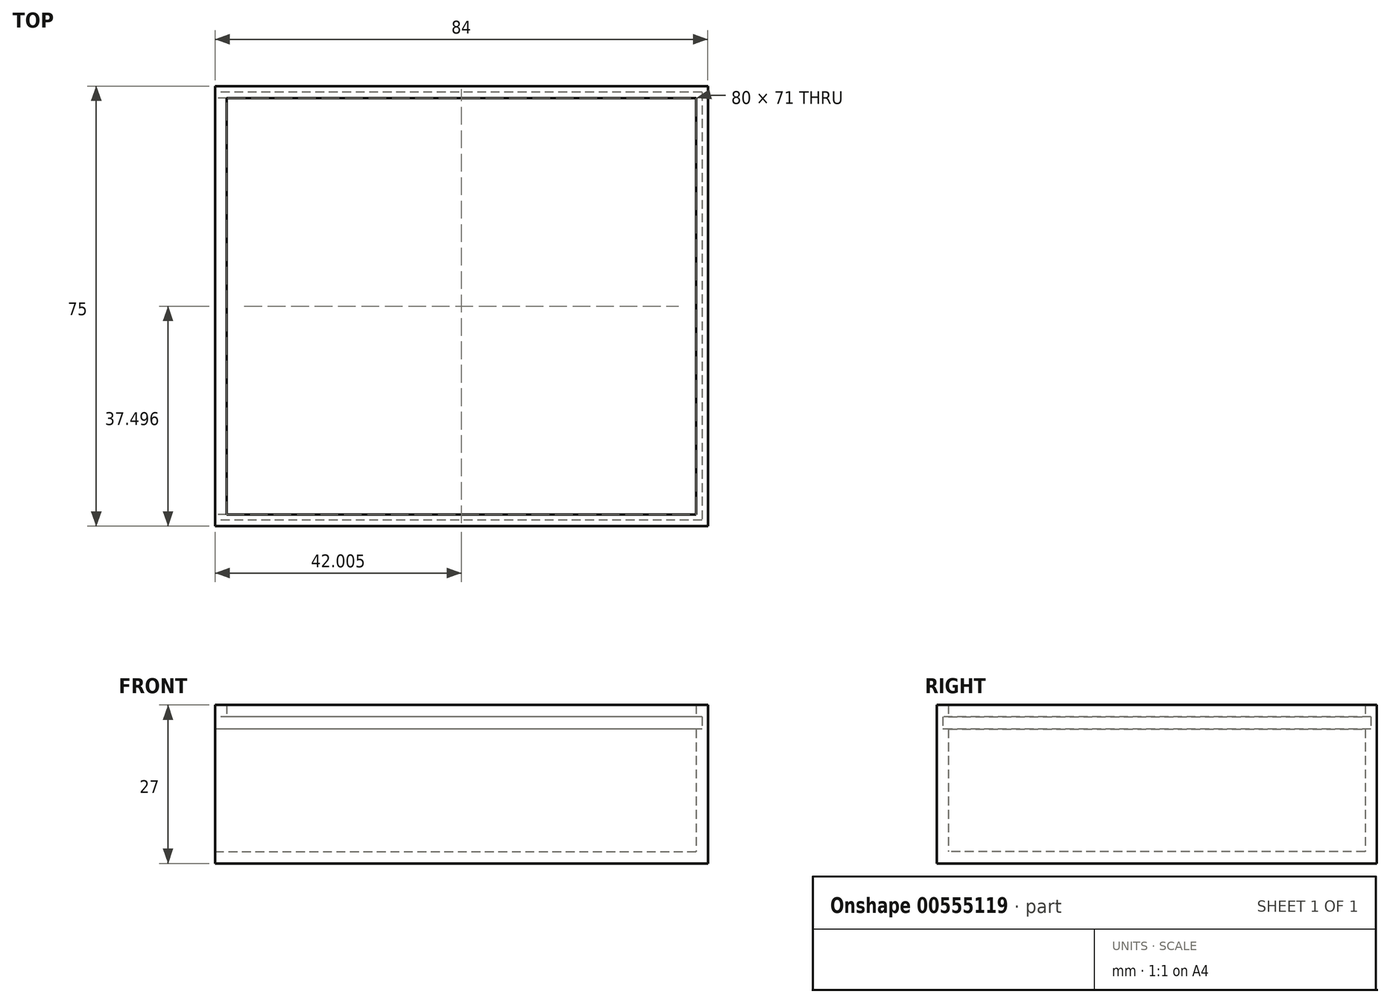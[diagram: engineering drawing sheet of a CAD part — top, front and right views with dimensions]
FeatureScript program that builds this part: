
annotation { "Feature Type Name" : "Feature", "Feature Type Description" : "" }
export const myFeature = defineFeature(function(context is Context, id is Id, definition is map)
    precondition{}
    {
        {
            var Q0;
            Q0=qCreatedBy(makeId("Top.planeOp"),FACE);
            var sketch = newSketch(context, id + "F0", { "sketchPlane" : qUnion([Q0])});
            skLineSegment(sketch, "E0.bottom", {"start": v(-44.93, -31.8) * mm, "end": v(39.07, -31.8) * mm});
            skLineSegment(sketch, "E0.top", {"start": v(-44.93, 43.2) * mm, "end": v(39.07, 43.2) * mm});
            skLineSegment(sketch, "E0.left", {"start": v(-44.93, -31.8) * mm, "end": v(-44.93, 43.2) * mm});
            skLineSegment(sketch, "E0.right", {"start": v(39.07, -31.8) * mm, "end": v(39.07, 43.2) * mm});
            skSolve(sketch);
        }
        {
            var Q0;
            Q0=makeQuery(id+"F0.imprint","IMPRINT",FACE,{"disambiguationData":[TD([[makeQuery(id+"F0.imprint","IMPRINT",EDGE,{"derivedFrom":sQuery(id+"F0.wireOp",EDGE,"E0.bottom")}),1.0]])]});
            extrude(context, id + "F1", {"entities" : qUnion([Q0]), "oppositeDirection" : true, "depth" : 2 * mm, "offsetDistance" : 25 * mm});
        }
        {
            var Q0;
            Q0=makeQuery(id+"F1.opExtrude","CAP_FACE",FACE,{"disambiguationData":[OSD([sQuery(id+"F0.wireOp",EDGE,"E0.bottom"),sQuery(id+"F0.wireOp",EDGE,"E0.top"),sQuery(id+"F0.wireOp",EDGE,"E0.left"),sQuery(id+"F0.wireOp",EDGE,"E0.right")])],"isStart":true});
            var sketch = newSketch(context, id + "F2", { "sketchPlane" : qUnion([Q0])});
            skLineSegment(sketch, "E1.bottom", {"start": v(-42.93, 41.2) * mm, "end": v(37.07, 41.2) * mm});
            skLineSegment(sketch, "E1.top", {"start": v(-42.93, -29.8) * mm, "end": v(37.07, -29.8) * mm});
            skLineSegment(sketch, "E1.left", {"start": v(-42.93, 41.2) * mm, "end": v(-42.93, -29.8) * mm});
            skLineSegment(sketch, "E1.right", {"start": v(37.07, 41.2) * mm, "end": v(37.07, -29.8) * mm});
            skSolve(sketch);
        }
        {
            var Q0;
            Q0=makeQuery(id+"F2.imprint","IMPRINT",FACE,{"disambiguationData":[TD([[makeQuery(id+"F2.imprint","IMPRINT",EDGE,{"derivedFrom":sQuery(id+"F2.wireOp",EDGE,"E1.bottom")}),1.0]])]});
            extrude(context, id + "F3", {"entities" : qUnion([Q0]), "operationType" : NewBodyOperationType.ADD, "depth" : 25 * mm, "offsetDistance" : 25 * mm});
        }
        {
            var Q0;
            {var subQ0=sQuery(id+"F0.wireOp",EDGE,"E0.left");Q0=makeQuery(id+"F3.boolean.opBoolean","MERGE",FACE,{"derivedFrom":[makeQuery(id+"F1.opExtrude","SWEPT_FACE",FACE,{"disambiguationData":[OSD([subQ0])]}),makeQuery(id+"F3.opExtrude","SWEPT_FACE",FACE,{"disambiguationData":[OSD([subQ0])]})]});}
            var sketch = newSketch(context, id + "F4", { "sketchPlane" : qUnion([Q0])});
            skLineSegment(sketch, "E2.bottom", {"start": v(-42.2, 23) * mm, "end": v(30.8, 23) * mm});
            skLineSegment(sketch, "E2.top", {"start": v(-42.2, 20.9) * mm, "end": v(30.8, 20.9) * mm});
            skLineSegment(sketch, "E2.left", {"start": v(-42.2, 23) * mm, "end": v(-42.2, 20.9) * mm});
            skLineSegment(sketch, "E2.right", {"start": v(30.8, 23) * mm, "end": v(30.8, 20.9) * mm});
            skSolve(sketch);
        }
        {
            var Q0;
            Q0=makeQuery(id+"F4.imprint","IMPRINT",FACE,{"disambiguationData":[TD([[makeQuery(id+"F4.imprint","IMPRINT",EDGE,{"derivedFrom":sQuery(id+"F4.wireOp",EDGE,"E2.bottom")}),-1.0]])]});
            extrude(context, id + "F5", {"entities" : qUnion([Q0]), "operationType" : NewBodyOperationType.REMOVE, "oppositeDirection" : true, "depth" : 83 * mm, "offsetDistance" : 25 * mm});
        }
        {
            var Q0;
            {var subQ0=sQuery(id+"F0.wireOp",EDGE,"E0.left");Q0=makeQuery(id+"F3.boolean.opBoolean","MERGE",FACE,{"derivedFrom":[makeQuery(id+"F1.opExtrude","SWEPT_FACE",FACE,{"disambiguationData":[OSD([subQ0])]}),makeQuery(id+"F3.opExtrude","SWEPT_FACE",FACE,{"disambiguationData":[OSD([subQ0])]})]});}
            var sketch = newSketch(context, id + "F6", { "sketchPlane" : qUnion([Q0])});
            skLineSegment(sketch, "E3.bottom", {"start": v(-41.2, 20.9) * mm, "end": v(29.8, 20.9) * mm});
            skLineSegment(sketch, "E3.top", {"start": v(-41.2, 0) * mm, "end": v(29.8, 0) * mm});
            skLineSegment(sketch, "E3.left", {"start": v(-41.2, 20.9) * mm, "end": v(-41.2, 0) * mm});
            skLineSegment(sketch, "E3.right", {"start": v(29.8, 20.9) * mm, "end": v(29.8, 0) * mm});
            skSolve(sketch);
        }
        {
            var Q0;
            Q0=makeQuery(id+"F6.imprint","IMPRINT",FACE,{"disambiguationData":[TD([[makeQuery(id+"F6.imprint","IMPRINT",EDGE,{"derivedFrom":sQuery(id+"F6.wireOp",EDGE,"E3.bottom")}),-1.0]])]});
            extrude(context, id + "F7", {"entities" : qUnion([Q0]), "operationType" : NewBodyOperationType.REMOVE, "oppositeDirection" : true, "depth" : 2 * mm, "offsetDistance" : 25 * mm});
        }
    });
